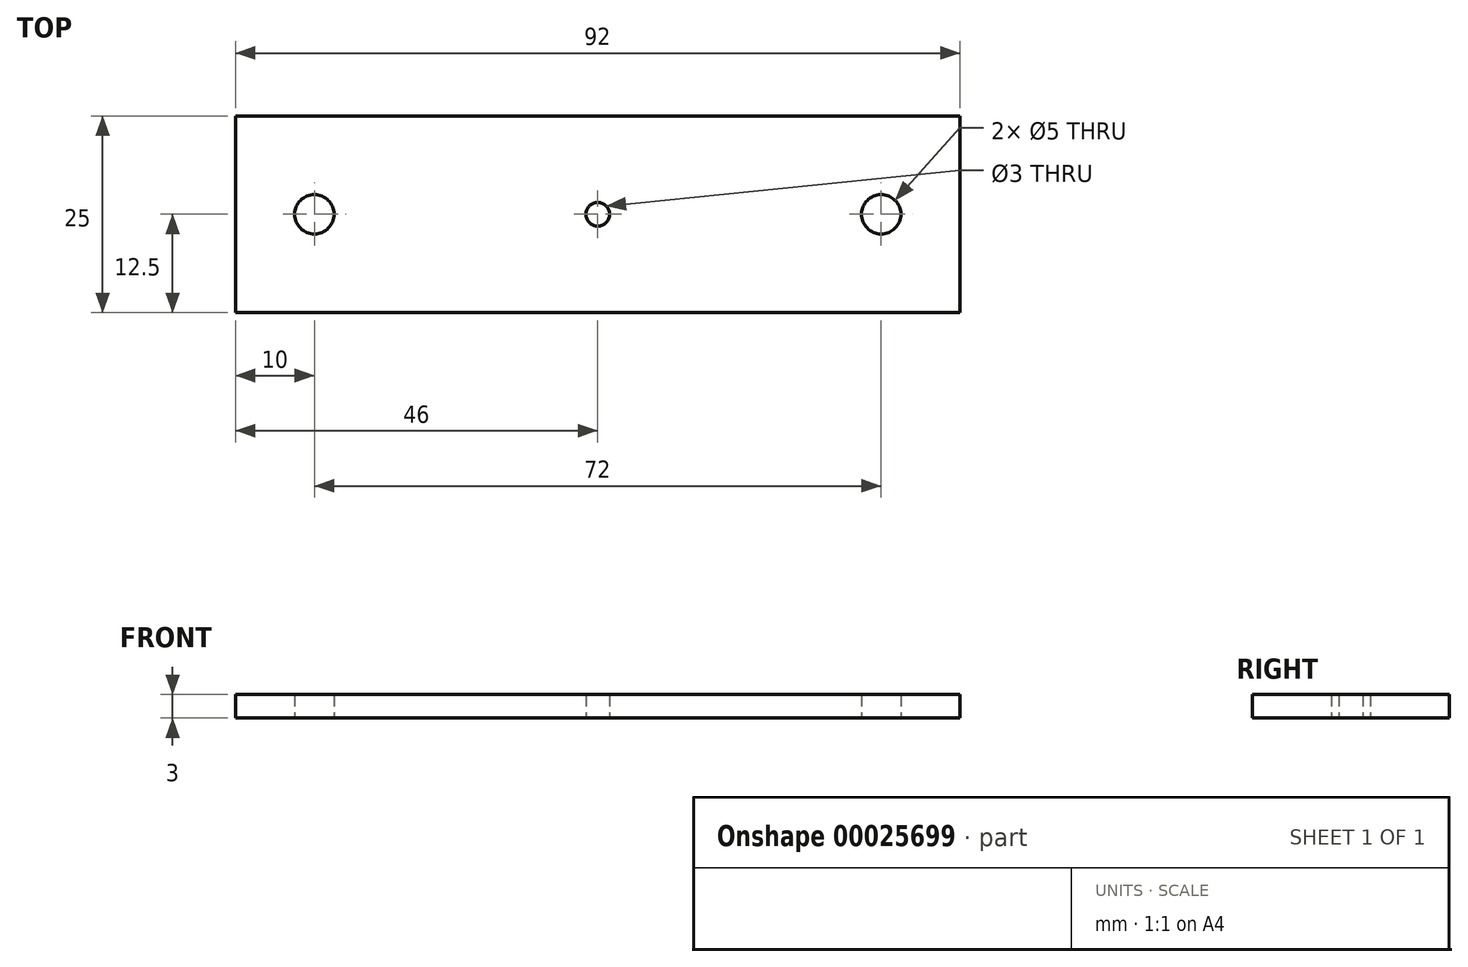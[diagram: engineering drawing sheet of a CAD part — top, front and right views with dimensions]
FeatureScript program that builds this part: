
annotation { "Feature Type Name" : "Feature", "Feature Type Description" : "" }
export const myFeature = defineFeature(function(context is Context, id is Id, definition is map)
    precondition{}
    {
        {
            var Q0;
            Q0=qCreatedBy(makeId("Top.planeOp"),FACE);
            var sketch = newSketch(context, id + "F0", { "sketchPlane" : qUnion([Q0])});
            skLineSegment(sketch, "E0.bottom", {"start": v(46, 12.5) * mm, "end": v(-46, 12.5) * mm});
            skLineSegment(sketch, "E0.top", {"start": v(46, -12.5) * mm, "end": v(-46, -12.5) * mm});
            skLineSegment(sketch, "E0.left", {"start": v(46, 12.5) * mm, "end": v(46, -12.5) * mm});
            skLineSegment(sketch, "E0.right", {"start": v(-46, 12.5) * mm, "end": v(-46, -12.5) * mm});
            skPoint(sketch, "E0.middle", {"position": v(0, 0) * mm});
            skCircle(sketch, "E1", {"center": v(0, 0) * mm, "radius": 1.5 * mm});
            skCircle(sketch, "E2", {"center": v(-36, 0) * mm, "radius": 2.5 * mm});
            skCircle(sketch, "E3", {"center": v(36, 0) * mm, "radius": 2.5 * mm});
            skLineSegment(sketch, "E4", {"start": v(0, 0) * mm, "end": v(-36, 0) * mm, "construction": true});
            skLineSegment(sketch, "E5", {"start": v(0, 0) * mm, "end": v(36, 0) * mm, "construction": true});
            skLineSegment(sketch, "E6", {"start": v(0, 0) * mm, "end": v(0, 12.5) * mm});
            skSolve(sketch);
        }
        {
            var Q0;
            Q0=qSketchRegion(id+"F0",true);
            extrude(context, id + "F1", {"entities" : qUnion([Q0]), "depth" : 3 * mm});
        }
    });
